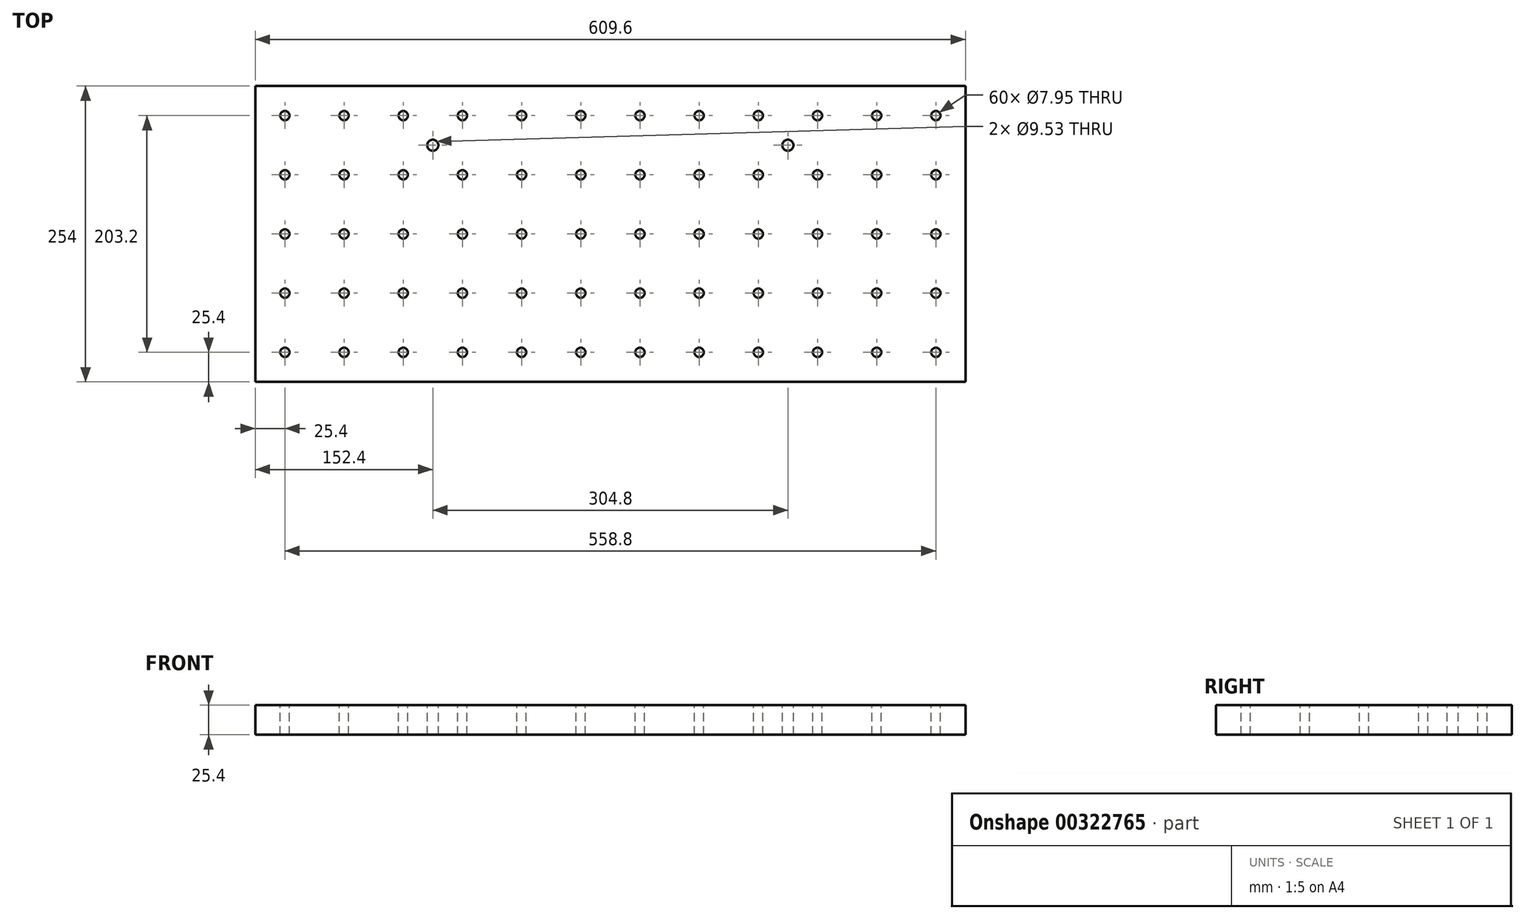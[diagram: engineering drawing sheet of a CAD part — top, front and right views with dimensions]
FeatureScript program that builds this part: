
annotation { "Feature Type Name" : "Feature", "Feature Type Description" : "" }
export const myFeature = defineFeature(function(context is Context, id is Id, definition is map)
    precondition{}
    {
        {
            var Q0;
            Q0=qCreatedBy(makeId("Top.planeOp"),FACE);
            var sketch = newSketch(context, id + "F0", { "sketchPlane" : qUnion([Q0])});
            skLineSegment(sketch, "E0.bottom", {"start": v(-304.8, 127) * mm, "end": v(304.8, 127) * mm});
            skLineSegment(sketch, "E0.top", {"start": v(-304.8, -127) * mm, "end": v(304.8, -127) * mm});
            skLineSegment(sketch, "E0.left", {"start": v(-304.8, 127) * mm, "end": v(-304.8, -127) * mm});
            skLineSegment(sketch, "E0.right", {"start": v(304.8, 127) * mm, "end": v(304.8, -127) * mm});
            skPoint(sketch, "E0.middle", {"position": v(0, 0) * mm});
            skCircle(sketch, "E1", {"center": v(-279.4, 101.6) * mm, "radius": 3.98 * mm});
            skCircle(sketch, "E2.0.1.0", {"center": v(-279.4, 50.8) * mm, "radius": 3.98 * mm});
            skCircle(sketch, "E2.0.2.0", {"center": v(-279.4, 0) * mm, "radius": 3.98 * mm});
            skCircle(sketch, "E2.0.3.0", {"center": v(-279.4, -50.8) * mm, "radius": 3.98 * mm});
            skCircle(sketch, "E2.0.4.0", {"center": v(-279.4, -101.6) * mm, "radius": 3.98 * mm});
            skCircle(sketch, "E2.1.0.0", {"center": v(-228.6, 101.6) * mm, "radius": 3.98 * mm});
            skCircle(sketch, "E2.1.1.0", {"center": v(-228.6, 50.8) * mm, "radius": 3.98 * mm});
            skCircle(sketch, "E2.1.2.0", {"center": v(-228.6, 0) * mm, "radius": 3.98 * mm});
            skCircle(sketch, "E2.1.3.0", {"center": v(-228.6, -50.8) * mm, "radius": 3.98 * mm});
            skCircle(sketch, "E2.1.4.0", {"center": v(-228.6, -101.6) * mm, "radius": 3.98 * mm});
            skCircle(sketch, "E2.2.0.0", {"center": v(-177.8, 101.6) * mm, "radius": 3.98 * mm});
            skCircle(sketch, "E2.2.1.0", {"center": v(-177.8, 50.8) * mm, "radius": 3.98 * mm});
            skCircle(sketch, "E2.2.2.0", {"center": v(-177.8, 0) * mm, "radius": 3.98 * mm});
            skCircle(sketch, "E2.2.3.0", {"center": v(-177.8, -50.8) * mm, "radius": 3.98 * mm});
            skCircle(sketch, "E2.2.4.0", {"center": v(-177.8, -101.6) * mm, "radius": 3.98 * mm});
            skCircle(sketch, "E2.3.0.0", {"center": v(-127, 101.6) * mm, "radius": 3.98 * mm});
            skCircle(sketch, "E2.3.1.0", {"center": v(-127, 50.8) * mm, "radius": 3.98 * mm});
            skCircle(sketch, "E2.3.2.0", {"center": v(-127, 0) * mm, "radius": 3.98 * mm});
            skCircle(sketch, "E2.3.3.0", {"center": v(-127, -50.8) * mm, "radius": 3.98 * mm});
            skCircle(sketch, "E2.3.4.0", {"center": v(-127, -101.6) * mm, "radius": 3.98 * mm});
            skCircle(sketch, "E2.4.0.0", {"center": v(-76.2, 101.6) * mm, "radius": 3.98 * mm});
            skCircle(sketch, "E2.4.1.0", {"center": v(-76.2, 50.8) * mm, "radius": 3.98 * mm});
            skCircle(sketch, "E2.4.2.0", {"center": v(-76.2, 0) * mm, "radius": 3.98 * mm});
            skCircle(sketch, "E2.4.3.0", {"center": v(-76.2, -50.8) * mm, "radius": 3.98 * mm});
            skCircle(sketch, "E2.4.4.0", {"center": v(-76.2, -101.6) * mm, "radius": 3.98 * mm});
            skCircle(sketch, "E2.5.0.0", {"center": v(-25.4, 101.6) * mm, "radius": 3.98 * mm});
            skCircle(sketch, "E2.5.1.0", {"center": v(-25.4, 50.8) * mm, "radius": 3.98 * mm});
            skCircle(sketch, "E2.5.2.0", {"center": v(-25.4, 0) * mm, "radius": 3.98 * mm});
            skCircle(sketch, "E2.5.3.0", {"center": v(-25.4, -50.8) * mm, "radius": 3.98 * mm});
            skCircle(sketch, "E2.5.4.0", {"center": v(-25.4, -101.6) * mm, "radius": 3.98 * mm});
            skCircle(sketch, "E2.6.0.0", {"center": v(25.4, 101.6) * mm, "radius": 3.98 * mm});
            skCircle(sketch, "E2.6.1.0", {"center": v(25.4, 50.8) * mm, "radius": 3.98 * mm});
            skCircle(sketch, "E2.6.2.0", {"center": v(25.4, 0) * mm, "radius": 3.98 * mm});
            skCircle(sketch, "E2.6.3.0", {"center": v(25.4, -50.8) * mm, "radius": 3.98 * mm});
            skCircle(sketch, "E2.6.4.0", {"center": v(25.4, -101.6) * mm, "radius": 3.98 * mm});
            skCircle(sketch, "E2.7.0.0", {"center": v(76.2, 101.6) * mm, "radius": 3.98 * mm});
            skCircle(sketch, "E2.7.1.0", {"center": v(76.2, 50.8) * mm, "radius": 3.98 * mm});
            skCircle(sketch, "E2.7.2.0", {"center": v(76.2, 0) * mm, "radius": 3.98 * mm});
            skCircle(sketch, "E2.7.3.0", {"center": v(76.2, -50.8) * mm, "radius": 3.98 * mm});
            skCircle(sketch, "E2.7.4.0", {"center": v(76.2, -101.6) * mm, "radius": 3.98 * mm});
            skCircle(sketch, "E2.8.0.0", {"center": v(127, 101.6) * mm, "radius": 3.98 * mm});
            skCircle(sketch, "E2.8.1.0", {"center": v(127, 50.8) * mm, "radius": 3.98 * mm});
            skCircle(sketch, "E2.8.2.0", {"center": v(127, 0) * mm, "radius": 3.98 * mm});
            skCircle(sketch, "E2.8.3.0", {"center": v(127, -50.8) * mm, "radius": 3.98 * mm});
            skCircle(sketch, "E2.8.4.0", {"center": v(127, -101.6) * mm, "radius": 3.98 * mm});
            skCircle(sketch, "E2.9.0.0", {"center": v(177.8, 101.6) * mm, "radius": 3.98 * mm});
            skCircle(sketch, "E2.9.1.0", {"center": v(177.8, 50.8) * mm, "radius": 3.98 * mm});
            skCircle(sketch, "E2.9.2.0", {"center": v(177.8, 0) * mm, "radius": 3.98 * mm});
            skCircle(sketch, "E2.9.3.0", {"center": v(177.8, -50.8) * mm, "radius": 3.98 * mm});
            skCircle(sketch, "E2.9.4.0", {"center": v(177.8, -101.6) * mm, "radius": 3.98 * mm});
            skCircle(sketch, "E2.10.0.0", {"center": v(228.6, 101.6) * mm, "radius": 3.98 * mm});
            skCircle(sketch, "E2.10.1.0", {"center": v(228.6, 50.8) * mm, "radius": 3.98 * mm});
            skCircle(sketch, "E2.10.2.0", {"center": v(228.6, 0) * mm, "radius": 3.98 * mm});
            skCircle(sketch, "E2.10.3.0", {"center": v(228.6, -50.8) * mm, "radius": 3.98 * mm});
            skCircle(sketch, "E2.10.4.0", {"center": v(228.6, -101.6) * mm, "radius": 3.98 * mm});
            skCircle(sketch, "E2.11.0.0", {"center": v(279.4, 101.6) * mm, "radius": 3.98 * mm});
            skCircle(sketch, "E2.11.1.0", {"center": v(279.4, 50.8) * mm, "radius": 3.98 * mm});
            skCircle(sketch, "E2.11.2.0", {"center": v(279.4, 0) * mm, "radius": 3.98 * mm});
            skCircle(sketch, "E2.11.3.0", {"center": v(279.4, -50.8) * mm, "radius": 3.98 * mm});
            skCircle(sketch, "E2.11.4.0", {"center": v(279.4, -101.6) * mm, "radius": 3.98 * mm});
            skLineSegment(sketch, "E3", {"start": v(-279.4, -101.6) * mm, "end": v(-304.8, -101.6) * mm, "construction": true});
            skLineSegment(sketch, "E4", {"start": v(-279.4, -101.6) * mm, "end": v(-279.4, -127) * mm, "construction": true});
            skLineSegment(sketch, "E5", {"start": v(-279.4, -101.6) * mm, "end": v(-228.6, -101.6) * mm, "construction": true});
            skLineSegment(sketch, "E6", {"start": v(-279.4, -101.6) * mm, "end": v(-279.4, -50.8) * mm, "construction": true});
            skLineSegment(sketch, "E7.0", {"start": v(152.4, 127) * mm, "end": v(152.4, 76.2) * mm, "construction": true});
            skCircle(sketch, "E8", {"center": v(-152.4, 76.2) * mm, "radius": 4.76 * mm});
            skCircle(sketch, "E9.MirrorC", {"center": v(152.4, 76.2) * mm, "radius": 4.76 * mm});
            skLineSegment(sketch, "E10.trimOffspring", {"start": v(152.4, 76.2) * mm, "end": v(304.8, 76.2) * mm, "construction": true});
            skSolve(sketch);
        }
        {
            var Q0;
            Q0 = qSketchRegion(id + "F0", true);
            extrude(context, id + "F1", {"entities" : qUnion([Q0]), "oppositeDirection" : true, "depth" : 25.4 * mm});
        }
    });
